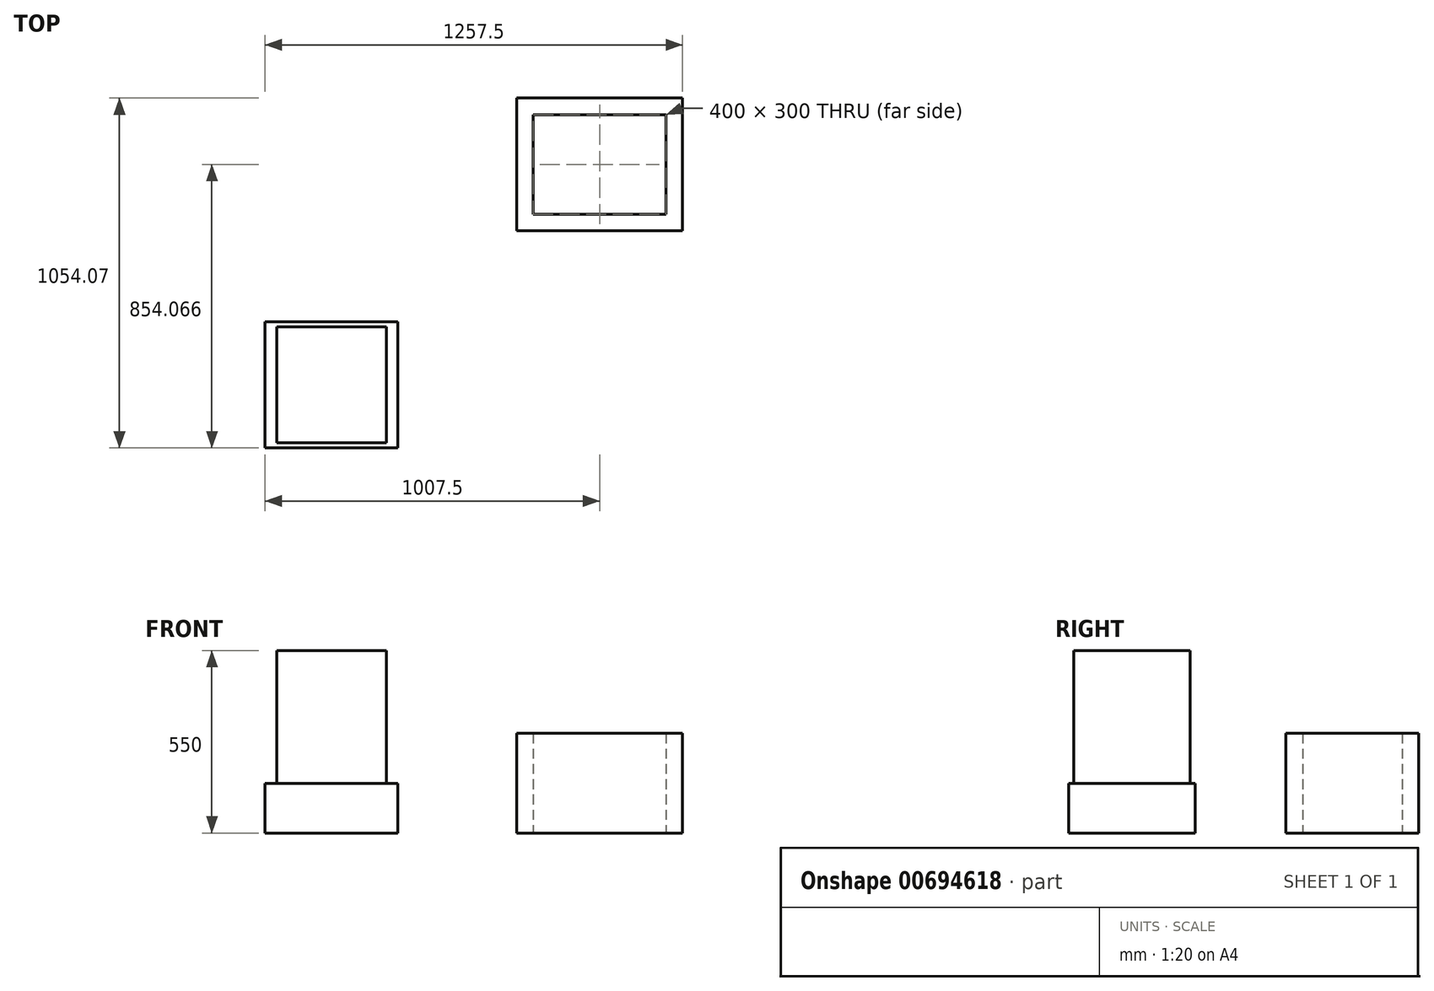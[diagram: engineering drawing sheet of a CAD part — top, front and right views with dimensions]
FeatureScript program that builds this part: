
annotation { "Feature Type Name" : "Feature", "Feature Type Description" : "" }
export const myFeature = defineFeature(function(context is Context, id is Id, definition is map)
    precondition{}
    {
        {
            var Q0;
            Q0=qCreatedBy(makeId("Top.planeOp"),FACE);
            var sketch = newSketch(context, id + "F0", { "sketchPlane" : qUnion([Q0])});
            skLineSegment(sketch, "E0.bottom", {"start": v(-307.1, 190.65) * mm, "end": v(192.9, 190.65) * mm});
            skLineSegment(sketch, "E0.top", {"start": v(-307.1, -209.35) * mm, "end": v(192.9, -209.35) * mm});
            skLineSegment(sketch, "E0.left", {"start": v(-307.1, 190.65) * mm, "end": v(-307.1, -209.35) * mm});
            skLineSegment(sketch, "E0.right", {"start": v(192.9, 190.65) * mm, "end": v(192.9, -209.35) * mm});
            skSolve(sketch);
        }
        {
            var Q0;
            Q0 = qSketchRegion(id + "F0", true);
            extrude(context, id + "F1", {"entities" : qUnion([Q0]), "depth" : 300 * mm, "offsetDistance" : 25 * mm});
        }
        {
            var Q0;
            Q0=makeQuery(id+"F1.opExtrude","CAP_FACE",FACE,{"disambiguationData":[OSD([sQuery(id+"F0.wireOp",EDGE,"E0.bottom"),sQuery(id+"F0.wireOp",EDGE,"E0.top"),sQuery(id+"F0.wireOp",EDGE,"E0.left"),sQuery(id+"F0.wireOp",EDGE,"E0.right")])],"isStart":true});
            var Q1;
            Q1=makeQuery(id+"F1.opExtrude","CAP_FACE",FACE,{"disambiguationData":[OSD([sQuery(id+"F0.wireOp",EDGE,"E0.bottom"),sQuery(id+"F0.wireOp",EDGE,"E0.top"),sQuery(id+"F0.wireOp",EDGE,"E0.left"),sQuery(id+"F0.wireOp",EDGE,"E0.right")])],"isStart":false});
            shell(context, id + "F2", {"entities" : qUnion([Q0, Q1]), "thickness" : 50 * mm});
        }
        {
            var Q0;
            Q0=qCreatedBy(makeId("Top.planeOp"),FACE);
            var sketch = newSketch(context, id + "F3", { "sketchPlane" : qUnion([Q0])});
            skLineSegment(sketch, "E1.bottom", {"start": v(-1064.6, -483.42) * mm, "end": v(-664.6, -483.42) * mm});
            skLineSegment(sketch, "E1.top", {"start": v(-1064.6, -863.42) * mm, "end": v(-664.6, -863.42) * mm});
            skLineSegment(sketch, "E1.left", {"start": v(-1064.6, -483.42) * mm, "end": v(-1064.6, -863.42) * mm});
            skLineSegment(sketch, "E1.right", {"start": v(-664.6, -483.42) * mm, "end": v(-664.6, -863.42) * mm});
            skSolve(sketch);
        }
        {
            var Q0;
            Q0 = qSketchRegion(id + "F3", true);
            extrude(context, id + "F4", {"entities" : qUnion([Q0]), "depth" : 150 * mm, "offsetDistance" : 25 * mm});
        }
        {
            var Q0;
            Q0=makeQuery(id+"F4.opExtrude","CAP_FACE",FACE,{"disambiguationData":[OSD([sQuery(id+"F3.wireOp",EDGE,"E1.bottom"),sQuery(id+"F3.wireOp",EDGE,"E1.top"),sQuery(id+"F3.wireOp",EDGE,"E1.left"),sQuery(id+"F3.wireOp",EDGE,"E1.right")])],"isStart":false});
            var sketch = newSketch(context, id + "F5", { "sketchPlane" : qUnion([Q0])});
            skLineSegment(sketch, "E2.bottom", {"start": v(-1029.6, -498.42) * mm, "end": v(-699.6, -498.42) * mm});
            skLineSegment(sketch, "E2.top", {"start": v(-1029.6, -848.42) * mm, "end": v(-699.6, -848.42) * mm});
            skLineSegment(sketch, "E2.left", {"start": v(-1029.6, -498.42) * mm, "end": v(-1029.6, -848.42) * mm});
            skLineSegment(sketch, "E2.right", {"start": v(-699.6, -498.42) * mm, "end": v(-699.6, -848.42) * mm});
            skSolve(sketch);
        }
        {
            var Q0;
            Q0=makeQuery(id+"F5.imprint","IMPRINT",FACE,{"disambiguationData":[TD([[makeQuery(id+"F5.imprint","IMPRINT",EDGE,{"derivedFrom":sQuery(id+"F5.wireOp",EDGE,"E2.bottom")}),-1.0]])]});
            extrude(context, id + "F6", {"entities" : qUnion([Q0]), "operationType" : NewBodyOperationType.ADD, "depth" : 400 * mm, "offsetDistance" : 25 * mm});
        }
    });
